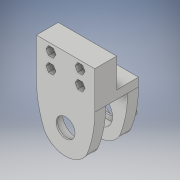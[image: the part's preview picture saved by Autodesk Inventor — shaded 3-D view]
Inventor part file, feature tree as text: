
AUTODESK INVENTOR PART (.ipt)
format: ipt  version: 2019 (Build 230136000, 136)  size: 317,952 bytes
history: native  units: mm
features: sketch x13, extrude x10, chamfer x5, hole x3, plane x1, fillet x1
ambient origin geometry x8: Origin, YZ Plane, XZ Plane, XY Plane, X Axis, Y Axis, Z Axis, Center Point
bodies: Solid1 (feature_tree)
feature tree (33):
  extrude  "Extrusion1"  Depth=20.0mm
  extrude  "Extrusion2"  Depth=40.0mm
  hole  "Hole1"  [1 undecoded]
  plane  "Work Plane1"
  extrude  "Extrusion3"  Depth=30.0mm TaperAngle=360.0deg
  extrude  "Extrusion4"  Depth=15.0mm TaperAngle=0.0deg
  hole  "Hole2"  [1 undecoded]
  extrude  "Extrusion5"  Depth=10.0mm
  extrude  "Extrusion6"  Depth=5.9mm
  chamfer  "Chamfer2"  Distance=3.5mm
  fillet  "Fillet1"  Radius=17.0mm
  extrude  "Extrusion7"  Depth=10.0mm TaperAngle=45.0deg
  chamfer  "Chamfer3"  Distance=10.0mm
  chamfer  "Chamfer4"  Distance=9.17mm Angle=45.0deg
  extrude  "Extrusion8"  Depth=4.0mm TaperAngle=45.0deg
  extrude  "Extrusion9"  Depth=1.0mm TaperAngle=0.0deg
  chamfer  "Chamfer5"  Distance=1.0mm
  hole  "Hole3"  [1 undecoded]
  extrude  "Extrusion10"  Depth=10.0mm
  chamfer  "Chamfer6"  Distance=10.0mm
  sketch  "Sketch1"  dims[d0=19.5mm d2=20.0mm]
  sketch  "Sketch2"  dims[d3=45.0mm d4=40.0mm]
  sketch  "Sketch3"  dims[d5=30.0mm d6=0.0mm d7=25.0mm]
  sketch  "Sketch4"  dims[d8=6.0mm d9=30.0mm d11=360.0deg]
  sketch  "Sketch5"  dims[d13=3.5mm d14=0.0mm]
  sketch  "Sketch6"  dims[d15=3.9mm d16=6.0mm d17=5.0mm d18=5.0mm d19=90.0deg d20=10.0mm d21=0.0mm d22=15.0mm d23=0.0mm]
  sketch  "Sketch7"  dims[d27=20.0mm d28=15.0mm d29=0.0mm]
  sketch  "Sketch8"  dims[d30=20.0mm]
  sketch  "Sketch10"  dims[d31=3.75mm d32=6.0mm d33=4.0mm d34=2.0mm d35=90.0deg d36=10.0mm d37=90.0deg d38=5.9mm]
  sketch  "Sketch11"  dims[d39=5.9mm d40=5.9mm]
  sketch  "Sketch12"  dims[d41=5.9mm d42=3.5mm d43=0.0mm d44=17.0mm]
  sketch  "Sketch13"  dims[d45=10.0mm d46=0.0mm d47=8.25mm d48=2.0mm d49=45.0deg]
  sketch  "Sketch14"  dims[d50=74.25mm d51=10.0mm d52=0.0mm d53=9.17mm d54=2.0mm d55=45.0deg d56=4.0mm d57=2.0mm d58=45.0deg d59=1.0mm d60=0.0mm d61=1.0mm d62=0.0mm d63=2.0mm d64=2.0mm d65=45.0deg d66=13.0mm d67=6.0mm d68=10.0mm d69=7.0mm d70=90.0deg d71=8.0mm d72=20.594885mm d73=1.5mm d74=10.0mm d75=0.0mm d76=4.66mm d77=2.0mm d78=45.0deg]
note: 3 required parameter values undecoded (feature->parameter linkage not recoverable at this tier; creation-order binding heuristic only, values carry confidence <= 0.55)
